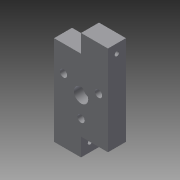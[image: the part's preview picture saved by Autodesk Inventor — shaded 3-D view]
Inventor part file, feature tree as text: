
AUTODESK INVENTOR PART (.ipt)
format: ipt  version: 2013 (Build 170138000, 138)  size: 121,856 bytes
history: native  units: in
note: dims shown in document units (in); Inventor stores cm internally (conversion verified against a paired STEP export)
features: extrude x7, sketch x7, reference x4
ambient origin geometry x8: Origin, YZ Plane, XZ Plane, XY Plane, X Axis, Y Axis, Z Axis, Center Point
bodies: Solid1 (feature_tree)
feature tree (18):
  extrude  "Extrusion1"  Depth=3.0in
  extrude  "Extrusion2"  Depth=0.75in
  extrude  "Extrusion3"  Depth=0.5in TaperAngle=0.0deg
  extrude  "Extrusion4"  Depth=0.5in
  extrude  "Extrusion5"  Depth=0.4in
  extrude  "Extrusion7"  Depth=0.125in
  extrude  "Extrusion9"  Depth=0.25in
  sketch  "Sketch1"  dims[d0=1.5in d1=3.0in]
  sketch  "Sketch2"  dims[d2=0.5in d3=0.0in d4=0.75in]
  sketch  "Sketch3"  dims[d5=0.5in d6=0.5in d7=0.0in]
  sketch  "Sketch4"  dims[d8=0.75in d9=0.5in]
  sketch  "Sketch5"  dims[d10=0.5in d11=0.0in d12=0.4in]
  sketch  "Sketch7"  dims[d13=0.25in d14=0.0in d16=0.125in]
  reference  "Reference1"
  reference  "Reference2"
  reference  "Reference3"
  sketch  "Sketch9"  dims[d17=0.25in d18=0.25in d19=0.25in d20=0.25in d21=0.75in d22=0.0in d29=0.25in d30=0.0in d34=0.125in d35=0.25in d36=0.2468in d37=0.2468in d38=0.75in d39=0.0in]
  reference  "Reference4"
